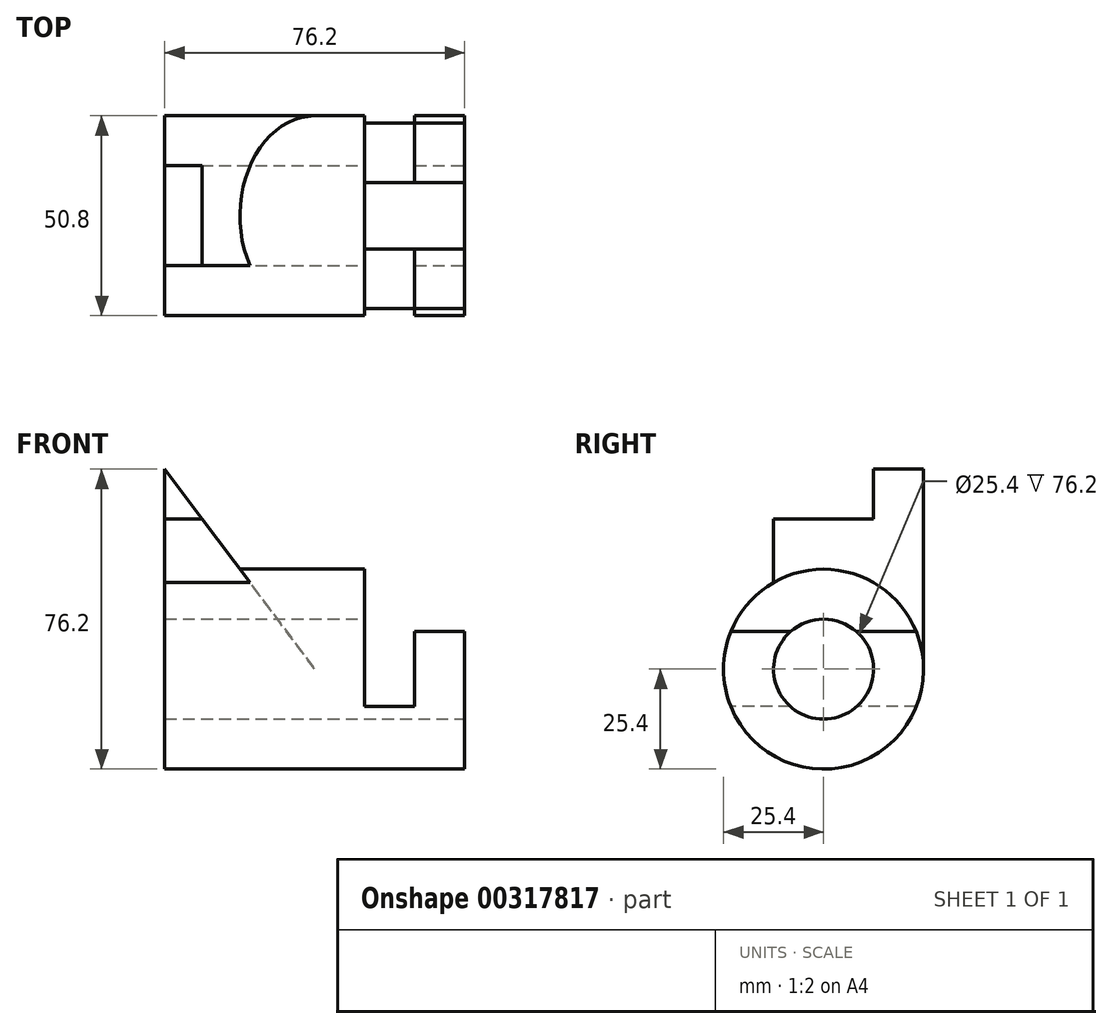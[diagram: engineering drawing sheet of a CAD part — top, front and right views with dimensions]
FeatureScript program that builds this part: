
annotation { "Feature Type Name" : "Feature", "Feature Type Description" : "" }
export const myFeature = defineFeature(function(context is Context, id is Id, definition is map)
    precondition{}
    {
        {
            var Q0;
            Q0=qCreatedBy(makeId("Right.planeOp"),FACE);
            var sketch = newSketch(context, id + "F0", { "sketchPlane" : qUnion([Q0])});
            skCircle(sketch, "E0", {"center": v(0, 0) * mm, "radius": 25.4 * mm});
            skSolve(sketch);
        }
        {
            var Q0;
            Q0 = qSketchRegion(id + "F0", true);
            extrude(context, id + "F1", {"entities" : qUnion([Q0]), "oppositeDirection" : true, "depth" : 76.2 * mm});
        }
        {
            var Q0;
            Q0=qCreatedBy(makeId("Front.planeOp"),FACE);
            var sketch = newSketch(context, id + "F2", { "sketchPlane" : qUnion([Q0])});
            skLineSegment(sketch, "E1", {"start": v(0, 25.4) * mm, "end": v(-25.4, 25.4) * mm});
            skLineSegment(sketch, "E2", {"start": v(-25.4, 25.4) * mm, "end": v(-25.4, -9.53) * mm});
            skLineSegment(sketch, "E3", {"start": v(-25.4, -9.53) * mm, "end": v(-12.7, -9.53) * mm});
            skLineSegment(sketch, "E4", {"start": v(-12.7, -9.53) * mm, "end": v(-12.7, 9.53) * mm});
            skLineSegment(sketch, "E5", {"start": v(-12.7, 9.53) * mm, "end": v(0, 9.53) * mm});
            skLineSegment(sketch, "E6", {"start": v(0, 9.53) * mm, "end": v(0, 25.4) * mm});
            skSolve(sketch);
        }
        {
            var Q0;
            Q0 = qSketchRegion(id + "F2", true);
            extrude(context, id + "F3", {"entities" : qUnion([Q0]), "operationType" : NewBodyOperationType.REMOVE, "endBound" : BoundingType.SYMMETRIC, "oppositeDirection" : true, "depth" : 50.8 * mm});
        }
        {
            var Q0;
            Q0=qCreatedBy(makeId("Front.planeOp"),FACE);
            var sketch = newSketch(context, id + "F4", { "sketchPlane" : qUnion([Q0])});
            skLineSegment(sketch, "E7", {"start": v(-76.2, 0) * mm, "end": v(-76.2, 50.8) * mm});
            skLineSegment(sketch, "E8", {"start": v(-76.2, 50.8) * mm, "end": v(-38.1, 0) * mm});
            skLineSegment(sketch, "E9", {"start": v(-38.1, 0) * mm, "end": v(-76.2, 0) * mm});
            skSolve(sketch);
        }
        {
            var Q0;
            Q0 = qSketchRegion(id + "F4", true);
            extrude(context, id + "F5", {"entities" : qUnion([Q0]), "operationType" : NewBodyOperationType.ADD, "depth" : 12.7 * mm, "hasSecondDirection" : true, "secondDirectionOppositeDirection" : true, "secondDirectionDepth" : 25.4 * mm});
        }
        {
            var Q0;
            Q0=makeQuery(id+"F5.boolean.opBoolean","MERGE",FACE,{"derivedFrom":[makeQuery(id+"F1.opExtrude","CAP_FACE",FACE,{"disambiguationData":[OSD([sQuery(id+"F0.wireOp",EDGE,"E0")])],"isStart":false}),makeQuery(id+"F5.opExtrude","SWEPT_FACE",FACE,{"disambiguationData":[OSD([sQuery(id+"F4.wireOp",EDGE,"E7")])]})]});
            var sketch = newSketch(context, id + "F6", { "sketchPlane" : qUnion([Q0])});
            skLineSegment(sketch, "E10.bottom", {"start": v(12.7, 50.8) * mm, "end": v(-12.7, 50.8) * mm});
            skLineSegment(sketch, "E10.top", {"start": v(12.7, 38.1) * mm, "end": v(-12.7, 38.1) * mm});
            skLineSegment(sketch, "E10.left", {"start": v(12.7, 50.8) * mm, "end": v(12.7, 38.1) * mm});
            skLineSegment(sketch, "E10.right", {"start": v(-12.7, 50.8) * mm, "end": v(-12.7, 38.1) * mm});
            skSolve(sketch);
        }
        {
            var Q0;
            Q0 = qSketchRegion(id + "F6", true);
            extrude(context, id + "F7", {"entities" : qUnion([Q0]), "operationType" : NewBodyOperationType.REMOVE, "endBound" : BoundingType.THROUGH_ALL, "oppositeDirection" : true, "depth" : 25.4 * mm});
        }
        {
            var Q0;
            Q0=makeQuery(id+"F1.opExtrude","CAP_FACE",FACE,{"disambiguationData":[OSD([sQuery(id+"F0.wireOp",EDGE,"E0")])],"isStart":true});
            var sketch = newSketch(context, id + "F8", { "sketchPlane" : qUnion([Q0])});
            skCircle(sketch, "E11", {"center": v(0, 0) * mm, "radius": 12.7 * mm});
            skSolve(sketch);
        }
        {
            var Q0;
            Q0 = qSketchRegion(id + "F8", true);
            extrude(context, id + "F9", {"entities" : qUnion([Q0]), "operationType" : NewBodyOperationType.REMOVE, "endBound" : BoundingType.THROUGH_ALL, "oppositeDirection" : true, "depth" : 25.4 * mm});
        }
    });
